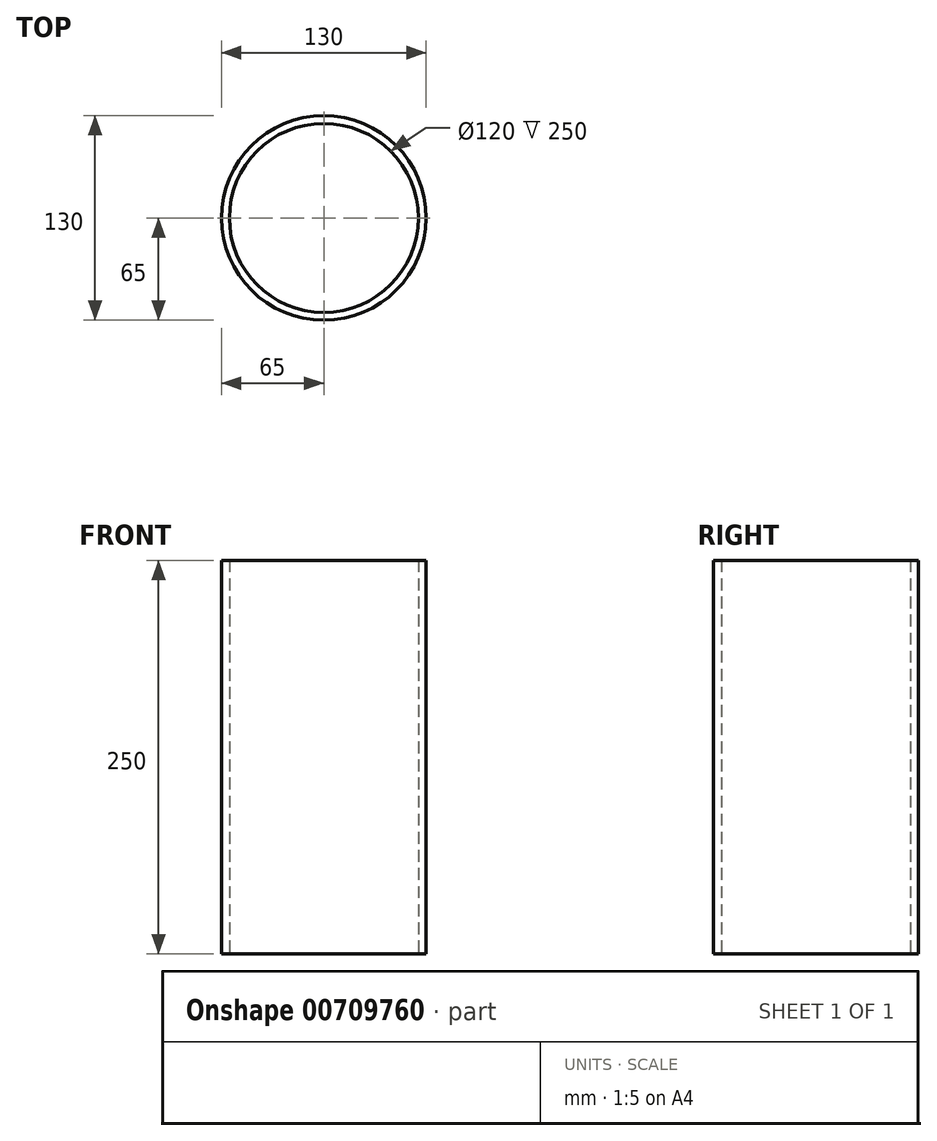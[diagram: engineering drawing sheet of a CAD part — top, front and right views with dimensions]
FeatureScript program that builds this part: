
annotation { "Feature Type Name" : "Feature", "Feature Type Description" : "" }
export const myFeature = defineFeature(function(context is Context, id is Id, definition is map)
    precondition{}
    {
        {
            var Q0;
            Q0=qCreatedBy(makeId("Top.planeOp"),FACE);
            var sketch = newSketch(context, id + "F0", { "sketchPlane" : qUnion([Q0])});
            skCircle(sketch, "E0", {"center": v(0, 0) * mm, "radius": 60 * mm});
            skCircle(sketch, "E1", {"center": v(0, 0) * mm, "radius": 65 * mm});
            skSolve(sketch);
        }
        {
            var Q0;
            Q0 = qSketchRegion(id + "F0", true);
            extrude(context, id + "F1", {"entities" : qUnion([Q0]), "depth" : 250 * mm, "offsetDistance" : 25 * mm});
        }
    });
